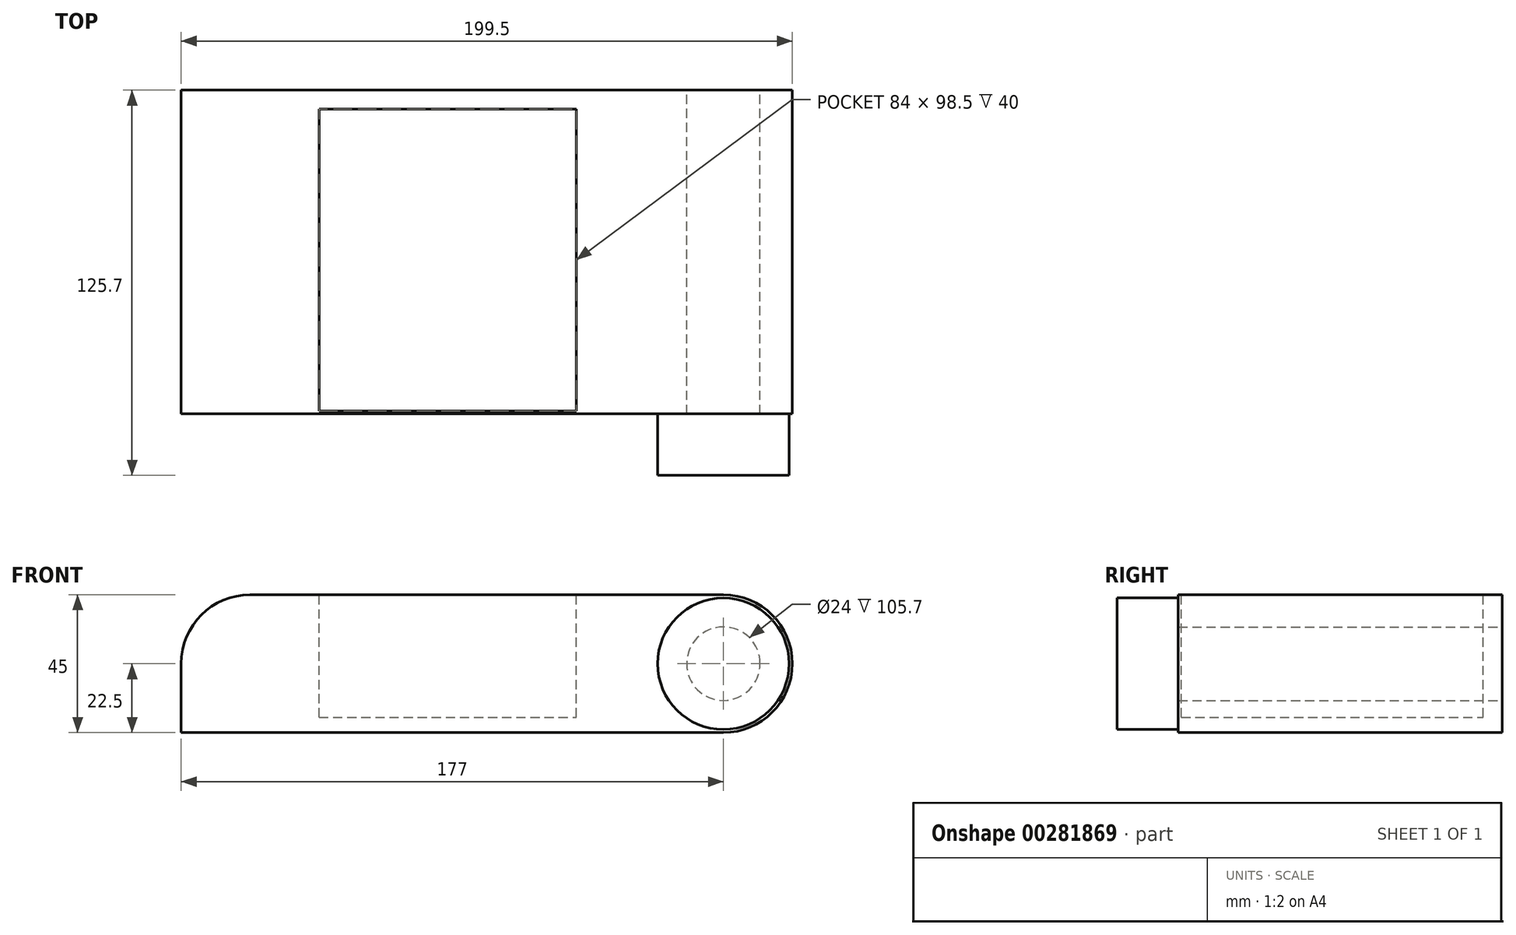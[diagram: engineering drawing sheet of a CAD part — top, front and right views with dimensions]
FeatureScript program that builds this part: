
annotation { "Feature Type Name" : "Feature", "Feature Type Description" : "" }
export const myFeature = defineFeature(function(context is Context, id is Id, definition is map)
    precondition{}
    {
        {
            var Q0;
            Q0=qCreatedBy(makeId("Front.planeOp"),FACE);
            var sketch = newSketch(context, id + "F0", { "sketchPlane" : qUnion([Q0])});
            skLineSegment(sketch, "E0.bottom", {"start": v(0, 22.5) * mm, "end": v(-64.5, 22.5) * mm});
            skLineSegment(sketch, "E0.top", {"start": v(0, -22.5) * mm, "end": v(-64.5, -22.5) * mm});
            skLineSegment(sketch, "E1.bottom", {"start": v(0, 22.5) * mm, "end": v(90, 22.5) * mm});
            skLineSegment(sketch, "E1.top", {"start": v(0, -22.5) * mm, "end": v(90, -22.5) * mm});
            skArc(sketch, "E2", {"start": v(-64.5, 22.5) * mm, "mid": v(-87, 0) * mm, "end": v(-64.5, -22.5) * mm});
            skArc(sketch, "E3", {"start": v(90, -22.5) * mm, "mid": v(112.5, 0) * mm, "end": v(90, 22.5) * mm});
            skCircle(sketch, "E4", {"center": v(-64.5, 0) * mm, "radius": 12 * mm, "construction": true});
            skCircle(sketch, "E5", {"center": v(90, 0) * mm, "radius": 12 * mm});
            skSolve(sketch);
        }
        {
            var Q0;
            Q0=qSketchRegion(id+"F0",true);
            extrude(context, id + "F1", {"entities" : qUnion([Q0]), "depth" : 105.7 * mm});
        }
        {
            var Q0;
            Q0=makeQuery(id+"F1.opExtrude","CAP_FACE",FACE,{"disambiguationData":[OSD([sQuery(id+"F0.wireOp",EDGE,"E0.bottom"),sQuery(id+"F0.wireOp",EDGE,"E0.top"),sQuery(id+"F0.wireOp",EDGE,"E1.bottom"),sQuery(id+"F0.wireOp",EDGE,"E1.top"),sQuery(id+"F0.wireOp",EDGE,"E2"),sQuery(id+"F0.wireOp",EDGE,"E3"),sQuery(id+"F0.wireOp",EDGE,"E4"),sQuery(id+"F0.wireOp",EDGE,"E5")])],"isStart":false});
            var sketch = newSketch(context, id + "F2", { "sketchPlane" : qUnion([Q0])});
            skLineSegment(sketch, "E6", {"start": v(-87, 0) * mm, "end": v(-87, -22.5) * mm});
            skLineSegment(sketch, "E7", {"start": v(-87, -22.5) * mm, "end": v(-64.5, -22.5) * mm});
            skLineSegment(sketch, "E8", {"start": v(-64.5, -22.5) * mm, "end": v(-70.42, -18.8) * mm});
            skLineSegment(sketch, "E9", {"start": v(-70.42, -18.8) * mm, "end": v(-80.16, -10.97) * mm});
            skLineSegment(sketch, "E10", {"start": v(-80.16, -10.97) * mm, "end": v(-84.27, -1.93) * mm});
            skLineSegment(sketch, "E11", {"start": v(-84.27, -1.93) * mm, "end": v(-87, 0) * mm});
            skSolve(sketch);
        }
        {
            var Q0;
            Q0=qSketchRegion(id+"F2",true);
            extrude(context, id + "F3", {"entities" : qUnion([Q0]), "operationType" : NewBodyOperationType.ADD, "oppositeDirection" : true, "depth" : 105.7 * mm});
        }
        {
            var Q0;
            Q0=makeQuery(id+"F1.opExtrude","SWEPT_FACE",FACE,{"disambiguationData":[OSD([sQuery(id+"F0.wireOp",EDGE,"E0.bottom"),sQuery(id+"F0.wireOp",EDGE,"E1.bottom")])]});
            var sketch = newSketch(context, id + "F4", { "sketchPlane" : qUnion([Q0])});
            skLineSegment(sketch, "E12.bottom", {"start": v(-42, -104.7) * mm, "end": v(42, -104.7) * mm});
            skLineSegment(sketch, "E12.top", {"start": v(-42, -6.2) * mm, "end": v(42, -6.2) * mm});
            skLineSegment(sketch, "E12.left", {"start": v(-42, -104.7) * mm, "end": v(-42, -6.2) * mm});
            skLineSegment(sketch, "E12.right", {"start": v(42, -104.7) * mm, "end": v(42, -6.2) * mm});
            skPoint(sketch, "E12.middle", {"position": v(0, -55.45) * mm});
            skSolve(sketch);
        }
        {
            var Q0;
            Q0 = qSketchRegion(id + "F4", true);
            extrude(context, id + "F5", {"entities" : qUnion([Q0]), "operationType" : NewBodyOperationType.REMOVE, "oppositeDirection" : true, "depth" : 40 * mm});
        }
        {
            var Q0;
            Q0=makeQuery(id+"F3.boolean.opBoolean","MERGE",FACE,{"derivedFrom":[makeQuery(id+"F1.opExtrude","CAP_FACE",FACE,{"disambiguationData":[OSD([sQuery(id+"F0.wireOp",EDGE,"E0.bottom"),sQuery(id+"F0.wireOp",EDGE,"E0.top"),sQuery(id+"F0.wireOp",EDGE,"E1.bottom"),sQuery(id+"F0.wireOp",EDGE,"E1.top"),sQuery(id+"F0.wireOp",EDGE,"E2"),sQuery(id+"F0.wireOp",EDGE,"E3"),sQuery(id+"F0.wireOp",EDGE,"E4"),sQuery(id+"F0.wireOp",EDGE,"E5")])],"isStart":false}),makeQuery(id+"F3.opExtrude","CAP_FACE",FACE,{"disambiguationData":[OSD([sQuery(id+"F2.wireOp",EDGE,"E6"),sQuery(id+"F2.wireOp",EDGE,"E7"),sQuery(id+"F2.wireOp",EDGE,"E8"),sQuery(id+"F2.wireOp",EDGE,"E9"),sQuery(id+"F2.wireOp",EDGE,"E10"),sQuery(id+"F2.wireOp",EDGE,"E11")])],"isStart":true})]});
            var sketch = newSketch(context, id + "F6", { "sketchPlane" : qUnion([Q0])});
            skCircle(sketch, "E13", {"center": v(90, 0) * mm, "radius": 21.46 * mm});
            skSolve(sketch);
        }
        {
            var Q0;
            Q0 = qSketchRegion(id + "F6", true);
            extrude(context, id + "F7", {"entities" : qUnion([Q0]), "operationType" : NewBodyOperationType.ADD, "depth" : 20 * mm});
        }
    });
